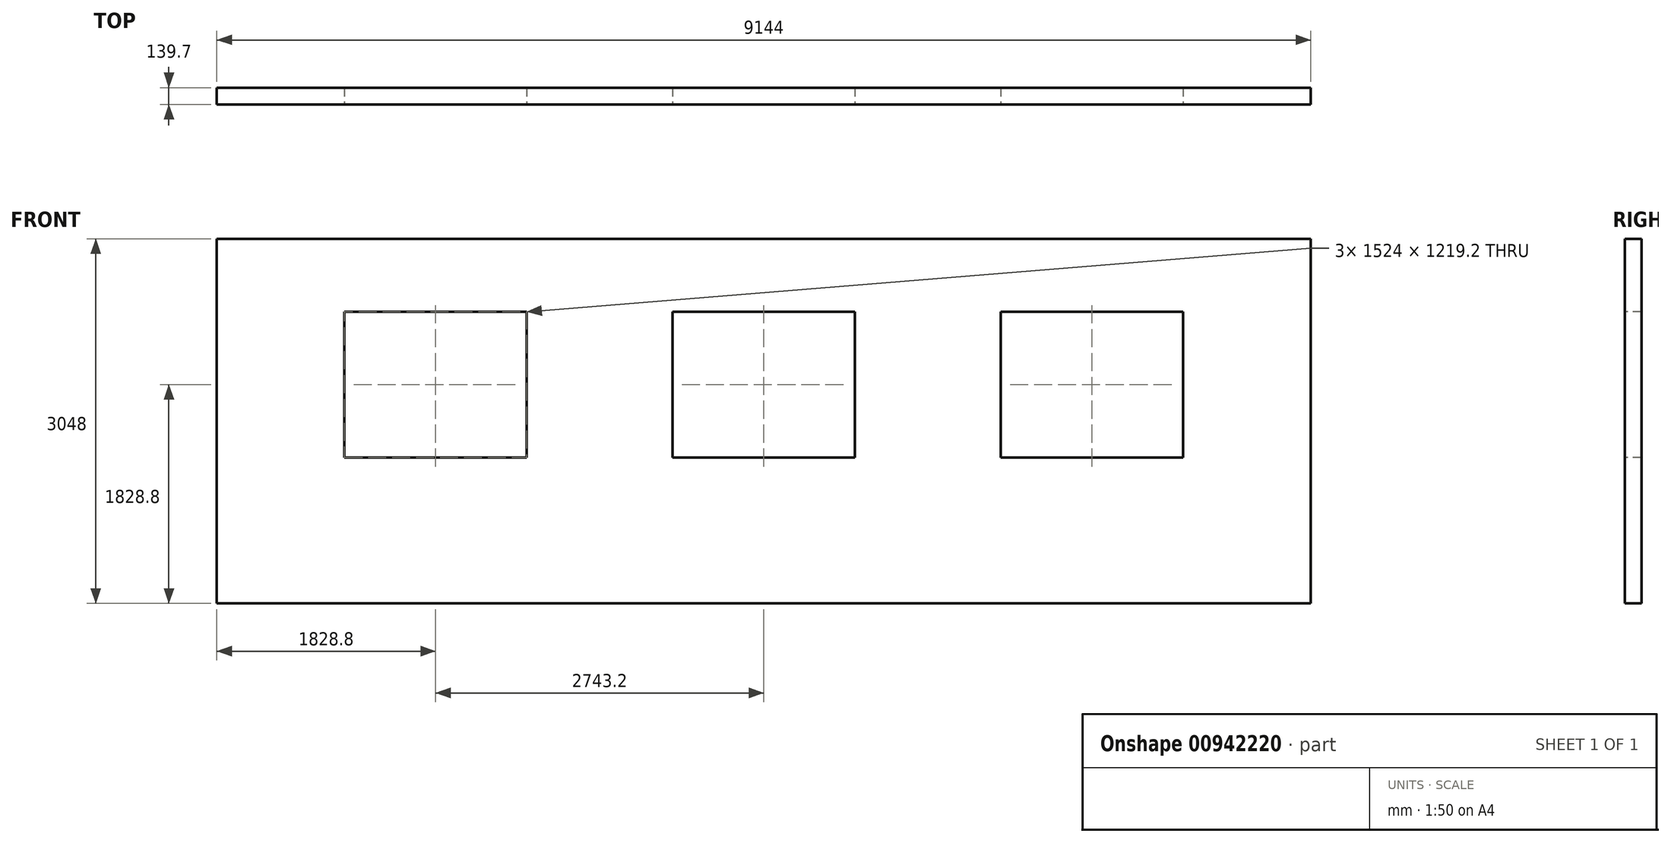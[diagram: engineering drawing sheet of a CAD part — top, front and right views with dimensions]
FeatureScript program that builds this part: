
annotation { "Feature Type Name" : "Feature", "Feature Type Description" : "" }
export const myFeature = defineFeature(function(context is Context, id is Id, definition is map)
    precondition{}
    {
        {
            var Q0;
            Q0=qCreatedBy(makeId("Front.planeOp"),FACE);
            var sketch = newSketch(context, id + "F0", { "sketchPlane" : qUnion([Q0])});
            skLineSegment(sketch, "E0.bottom", {"start": v(0, 0) * mm, "end": v(9144, 0) * mm});
            skLineSegment(sketch, "E0.top", {"start": v(0, 3048) * mm, "end": v(9144, 3048) * mm});
            skLineSegment(sketch, "E0.left", {"start": v(0, 0) * mm, "end": v(0, 3048) * mm});
            skLineSegment(sketch, "E0.right", {"start": v(9144, 0) * mm, "end": v(9144, 3048) * mm});
            skLineSegment(sketch, "E1.bottom", {"start": v(3810, 2438.4) * mm, "end": v(5334, 2438.4) * mm});
            skLineSegment(sketch, "E1.top", {"start": v(3810, 1219.2) * mm, "end": v(5334, 1219.2) * mm});
            skLineSegment(sketch, "E1.left", {"start": v(3810, 2438.4) * mm, "end": v(3810, 1219.2) * mm});
            skLineSegment(sketch, "E1.right", {"start": v(5334, 2438.4) * mm, "end": v(5334, 1219.2) * mm});
            skLineSegment(sketch, "E2.bottom", {"start": v(6553.2, 1219.2) * mm, "end": v(8077.2, 1219.2) * mm});
            skLineSegment(sketch, "E2.top", {"start": v(6553.2, 2438.4) * mm, "end": v(8077.2, 2438.4) * mm});
            skLineSegment(sketch, "E2.left", {"start": v(6553.2, 1219.2) * mm, "end": v(6553.2, 2438.4) * mm});
            skLineSegment(sketch, "E2.right", {"start": v(8077.2, 1219.2) * mm, "end": v(8077.2, 2438.4) * mm});
            skLineSegment(sketch, "E3.0", {"start": v(2590.8, 2438.4) * mm, "end": v(2590.8, 1219.2) * mm});
            skLineSegment(sketch, "E4.0", {"start": v(1066.8, 2438.4) * mm, "end": v(1066.8, 1219.2) * mm});
            skLineSegment(sketch, "E5", {"start": v(1066.8, 2438.4) * mm, "end": v(2590.8, 2438.4) * mm});
            skLineSegment(sketch, "E6", {"start": v(1066.8, 1219.2) * mm, "end": v(2590.8, 1219.2) * mm});
            skSolve(sketch);
        }
        {
            var Q0;
            Q0=makeQuery(id+"F0.imprint","IMPRINT",FACE,{"disambiguationData":[TD([[makeQuery(id+"F0.imprint","IMPRINT",EDGE,{"derivedFrom":sQuery(id+"F0.wireOp",EDGE,"E0.bottom")}),1.0]])]});
            extrude(context, id + "F1", {"entities" : qUnion([Q0]), "oppositeDirection" : true, "depth" : 139.7 * mm, "offsetDistance" : 25.4 * mm});
        }
    });
